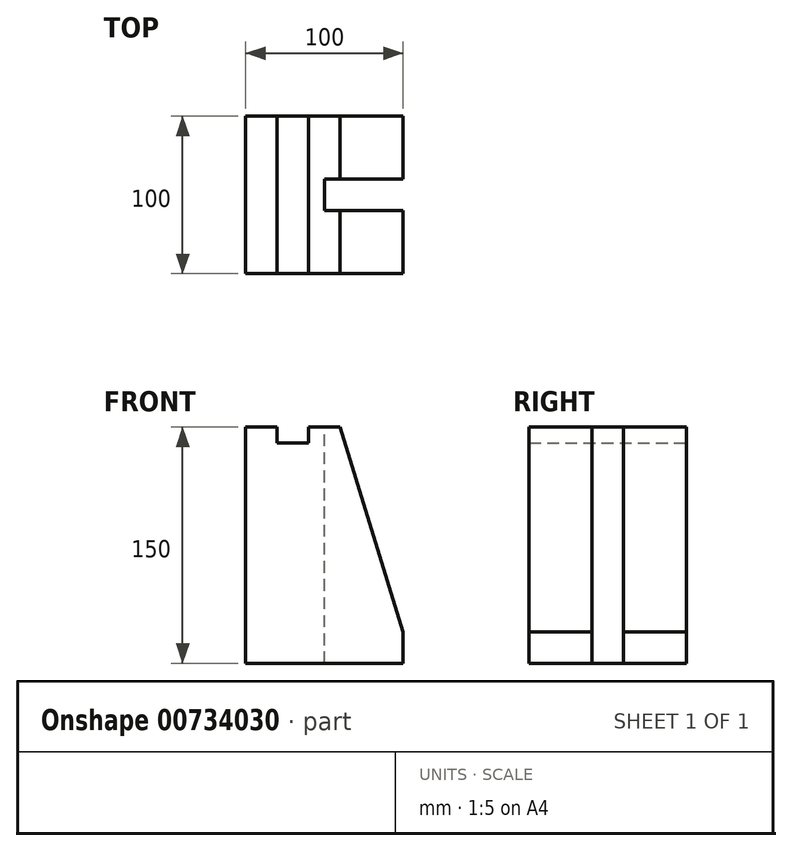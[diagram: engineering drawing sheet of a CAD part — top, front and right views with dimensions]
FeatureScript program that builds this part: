
annotation { "Feature Type Name" : "Feature", "Feature Type Description" : "" }
export const myFeature = defineFeature(function(context is Context, id is Id, definition is map)
    precondition{}
    {
        {
            var Q0;
            Q0=qCreatedBy(makeId("Front.planeOp"),FACE);
            var sketch = newSketch(context, id + "F0", { "sketchPlane" : qUnion([Q0])});
            skLineSegment(sketch, "E0", {"start": v(0, 0) * mm, "end": v(100, 0) * mm});
            skLineSegment(sketch, "E1", {"start": v(0, 0) * mm, "end": v(0, 150) * mm});
            skLineSegment(sketch, "E2", {"start": v(0, 150) * mm, "end": v(20, 150) * mm});
            skLineSegment(sketch, "E3", {"start": v(20, 150) * mm, "end": v(20, 140) * mm});
            skLineSegment(sketch, "E4", {"start": v(20, 140) * mm, "end": v(40, 140) * mm});
            skLineSegment(sketch, "E5", {"start": v(40, 140) * mm, "end": v(40, 150) * mm});
            skLineSegment(sketch, "E6", {"start": v(40, 150) * mm, "end": v(60, 150) * mm});
            skLineSegment(sketch, "E7", {"start": v(100, 0) * mm, "end": v(100, 20) * mm});
            skLineSegment(sketch, "E8", {"start": v(60, 150) * mm, "end": v(100, 20) * mm});
            skSolve(sketch);
        }
        {
            var Q0;
            Q0=makeQuery(id+"F0.imprint","IMPRINT",FACE,{"disambiguationData":[TD([[makeQuery(id+"F0.imprint","IMPRINT",EDGE,{"derivedFrom":sQuery(id+"F0.wireOp",EDGE,"E0")}),1.0]])]});
            extrude(context, id + "F1", {"entities" : qUnion([Q0]), "depth" : 100 * mm, "offsetDistance" : 25 * mm});
        }
        {
            var Q0;
            Q0=makeQuery(id+"F1.opExtrude","SWEPT_FACE",FACE,{"disambiguationData":[OSD([sQuery(id+"F0.wireOp",EDGE,"E6")])]});
            var sketch = newSketch(context, id + "F2", { "sketchPlane" : qUnion([Q0])});
            skLineSegment(sketch, "E9", {"start": v(60, -40) * mm, "end": v(50, -40) * mm});
            skLineSegment(sketch, "E10", {"start": v(50, -40) * mm, "end": v(50, -60) * mm});
            skLineSegment(sketch, "E11", {"start": v(50, -60) * mm, "end": v(60, -60) * mm});
            skLineSegment(sketch, "E12", {"start": v(60, -60) * mm, "end": v(60, -40) * mm});
            skLineSegment(sketch, "E13", {"start": v(60, -40) * mm, "end": v(100.06, -40) * mm});
            skLineSegment(sketch, "E14", {"start": v(100.06, -40) * mm, "end": v(100.06, -60) * mm});
            skLineSegment(sketch, "E15", {"start": v(100.06, -60) * mm, "end": v(60, -60) * mm});
            skLineSegment(sketch, "E16", {"start": v(60, -40) * mm, "end": v(60, -60) * mm});
            skSolve(sketch);
        }
        {
            var Q0;
            Q0=makeQuery(id+"F2.imprint","IMPRINT",FACE,{"disambiguationData":[TD([[makeQuery(id+"F2.imprint","IMPRINT",EDGE,{"derivedFrom":sQuery(id+"F2.wireOp",EDGE,"E13")}),-1.0]])]});
            var Q1;
            Q1=makeQuery(id+"F2.imprint","IMPRINT",FACE,{"disambiguationData":[TD([[makeQuery(id+"F2.imprint","IMPRINT",EDGE,{"derivedFrom":sQuery(id+"F2.wireOp",EDGE,"E9")}),1.0]])]});
            extrude(context, id + "F3", {"entities" : qUnion([Q0, Q1]), "operationType" : NewBodyOperationType.REMOVE, "oppositeDirection" : true, "depth" : 150 * mm, "offsetDistance" : 25 * mm});
        }
    });
